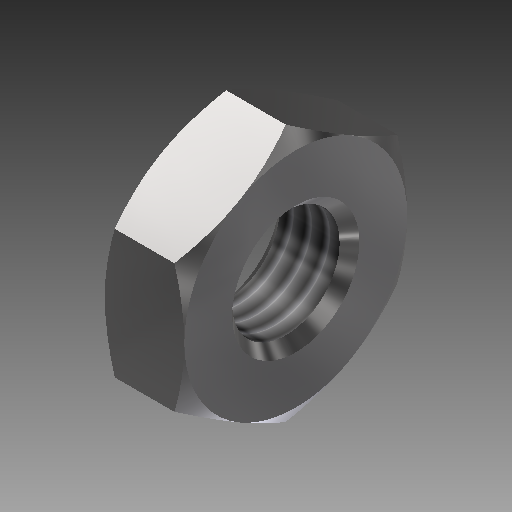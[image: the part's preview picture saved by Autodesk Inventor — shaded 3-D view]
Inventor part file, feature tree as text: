
AUTODESK INVENTOR PART (.ipt)
format: ipt  version: 2018 (Build 220112000, 112)  size: 178,176 bytes
history: native  units: in
note: dims shown in document units (in); Inventor stores cm internally (conversion verified against a paired STEP export)
features: other x8, revolve x2, sketch x2, extrude x1, thread x1
ambient origin geometry x8: Origin, YZ Plane, XZ Plane, XY Plane, X Axis, Y Axis, Z Axis, Center Point
bodies: Solid1 (feature_tree)
feature tree (14):
  extrude  "Extrusion1"  TaperAngle=360.0deg  [1 undecoded]
  revolve  "Revolution1"  Angle=360.0deg
  thread  "Thread1"  [1 undecoded]
  revolve  "Revolution2"  [1 undecoded]
  other  "conn_XY"
  other  "conn_YZ"
  other  "conn_ZX"
  other  "conn_X"
  other  "conn_Y"
  other  "conn_Z"
  other  "conn_Center"
  sketch  "Sketch_1"  dims[d0=0.156in d1=0.0in d2=360.0deg]
  other  "Fine_Thread"
  sketch  "Sketch_3"  dims[d3=0.1173in d4=0.0in d5=360.0deg d6=0.0in]
note: 3 required parameter values undecoded (feature->parameter linkage not recoverable at this tier; creation-order binding heuristic only, values carry confidence <= 0.55)
